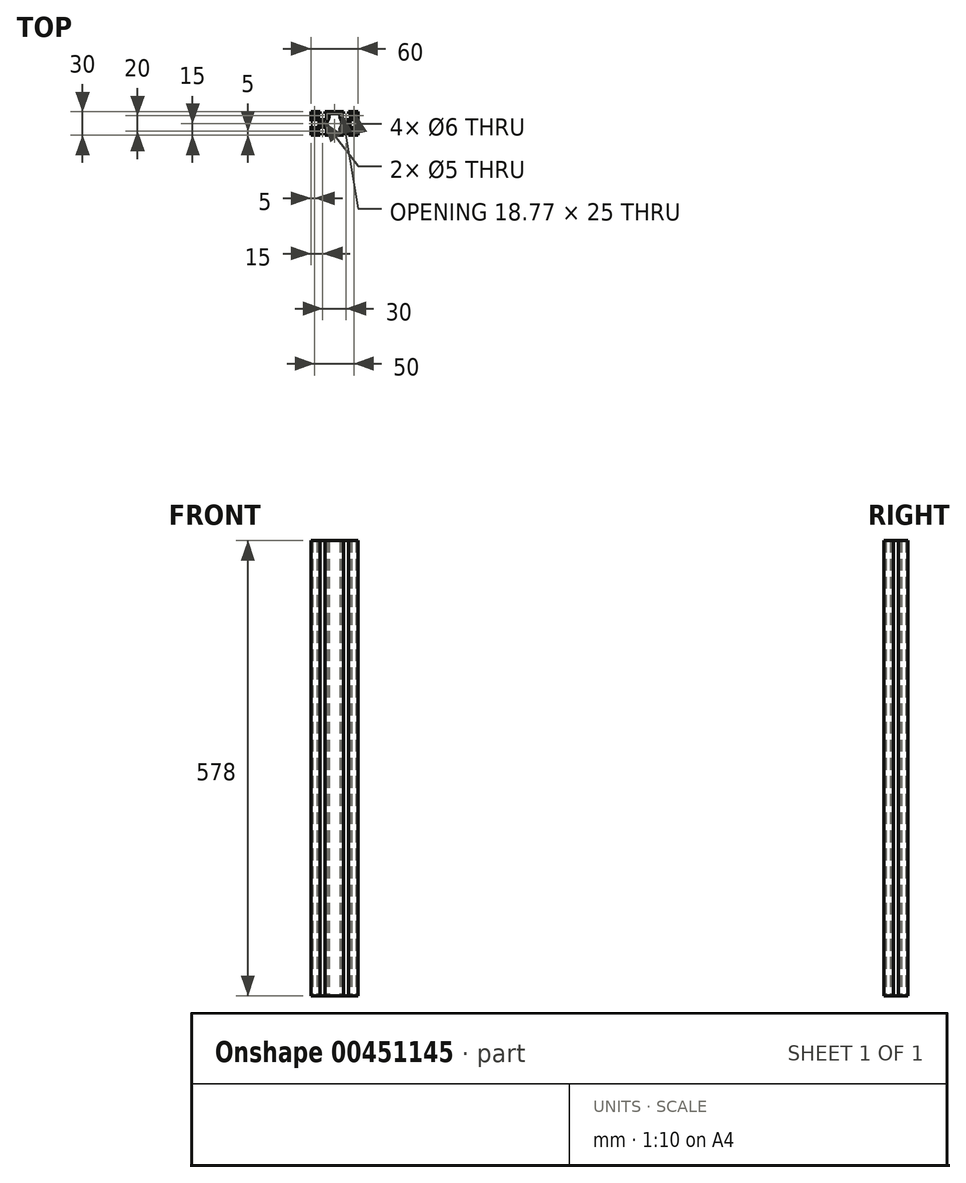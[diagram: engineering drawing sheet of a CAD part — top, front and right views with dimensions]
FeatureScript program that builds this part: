
annotation { "Feature Type Name" : "Feature", "Feature Type Description" : "" }
export const myFeature = defineFeature(function(context is Context, id is Id, definition is map)
    precondition{}
    {
        {
            var Q0;
            Q0=qCreatedBy(makeId("Top.planeOp"),FACE);
            var sketch = newSketch(context, id + "F0", { "sketchPlane" : qUnion([Q0])});
            skLineSegment(sketch, "E0.bottom", {"start": v(30, -15) * mm, "end": v(-30, -15) * mm});
            skLineSegment(sketch, "E0.top", {"start": v(30, 15) * mm, "end": v(-30, 15) * mm});
            skLineSegment(sketch, "E0.left", {"start": v(30, -15) * mm, "end": v(30, 15) * mm});
            skLineSegment(sketch, "E0.right", {"start": v(-30, -15) * mm, "end": v(-30, 15) * mm});
            skPoint(sketch, "E0.middle", {"position": v(0, 0) * mm});
            skLineSegment(sketch, "E1.top", {"start": v(-11.85, 15) * mm, "end": v(-18.15, 15) * mm});
            skLineSegment(sketch, "E1.left", {"start": v(-11.85, 12.5) * mm, "end": v(-11.85, 15) * mm});
            skLineSegment(sketch, "E1.right", {"start": v(-18.15, 12.5) * mm, "end": v(-18.15, 15) * mm});
            skPoint(sketch, "E1.middle", {"position": v(-15, 13.75) * mm});
            skLineSegment(sketch, "E2.bottom", {"start": v(-9.85, 12.5) * mm, "end": v(-11.85, 12.5) * mm});
            skLineSegment(sketch, "E2.left", {"start": v(-9.85, 12.5) * mm, "end": v(-9.85, 6.55) * mm});
            skLineSegment(sketch, "E2.right", {"start": v(-20.15, 12.5) * mm, "end": v(-20.15, 6.55) * mm});
            skPoint(sketch, "E2.middle", {"position": v(-15, 9.52) * mm});
            skArc(sketch, "E3", {"start": v(-20.15, 6.55) * mm, "mid": v(-15, 4.5) * mm, "end": v(-9.85, 6.55) * mm});
            skPoint(sketch, "E4.MirrorP", {"position": v(15, 9.52) * mm});
            skPoint(sketch, "E5.MirrorP", {"position": v(15, 13.75) * mm});
            skLineSegment(sketch, "E6.MirrorCS", {"start": v(11.85, 12.5) * mm, "end": v(11.85, 15) * mm});
            skLineSegment(sketch, "E7.MirrorCS", {"start": v(18.15, 12.5) * mm, "end": v(18.15, 15) * mm});
            skLineSegment(sketch, "E8.MirrorCS", {"start": v(9.85, 12.5) * mm, "end": v(11.85, 12.5) * mm});
            skLineSegment(sketch, "E9.MirrorCS", {"start": v(9.85, 12.5) * mm, "end": v(9.85, 6.55) * mm});
            skArc(sketch, "E10.MirrorCS", {"start": v(20.15, 6.55) * mm, "mid": v(15, 4.5) * mm, "end": v(9.85, 6.55) * mm});
            skLineSegment(sketch, "E11.MirrorCS", {"start": v(20.15, 12.5) * mm, "end": v(20.15, 6.55) * mm});
            skLineSegment(sketch, "E12.MirrorCS", {"start": v(11.85, 15) * mm, "end": v(18.15, 15) * mm});
            skLineSegment(sketch, "E13.trimOffspring", {"start": v(-18.15, 12.5) * mm, "end": v(-20.15, 12.5) * mm});
            skLineSegment(sketch, "E14.trimOffspring", {"start": v(18.15, 12.5) * mm, "end": v(20.15, 12.5) * mm});
            skCircle(sketch, "E15", {"center": v(-15, 0) * mm, "radius": 2.5 * mm});
            skCircle(sketch, "E16", {"center": v(-25, 10) * mm, "radius": 3 * mm});
            skCircle(sketch, "E17.MirrorC", {"center": v(25, 10) * mm, "radius": 3 * mm});
            skCircle(sketch, "E18.MirrorC", {"center": v(25, -10) * mm, "radius": 3 * mm});
            skCircle(sketch, "E19.MirrorC", {"center": v(-25, -10) * mm, "radius": 3 * mm});
            skCircle(sketch, "E20.MirrorC", {"center": v(15, 0) * mm, "radius": 2.5 * mm});
            skLineSegment(sketch, "E21", {"start": v(-7, 12.5) * mm, "end": v(0, 12.5) * mm});
            skLineSegment(sketch, "E22", {"start": v(-7, 12.5) * mm, "end": v(-7, 7) * mm});
            skLineSegment(sketch, "E23", {"start": v(-10, 0) * mm, "end": v(-7, 7) * mm});
            skLineSegment(sketch, "E24.MirrorCS", {"start": v(10, 0) * mm, "end": v(7, 7) * mm});
            skLineSegment(sketch, "E25.MirrorCS", {"start": v(7, 12.5) * mm, "end": v(0, 12.5) * mm});
            skLineSegment(sketch, "E26.MirrorCS", {"start": v(7, 12.5) * mm, "end": v(7, 7) * mm});
            skLineSegment(sketch, "E27.MirrorCS", {"start": v(-18.15, -12.5) * mm, "end": v(-20.15, -12.5) * mm});
            skLineSegment(sketch, "E28.MirrorCS", {"start": v(-9.85, -12.5) * mm, "end": v(-11.85, -12.5) * mm});
            skLineSegment(sketch, "E29.MirrorCS", {"start": v(-9.85, -12.5) * mm, "end": v(-9.85, -6.55) * mm});
            skPoint(sketch, "E30.MirrorP", {"position": v(-15, -13.75) * mm});
            skPoint(sketch, "E31.MirrorP", {"position": v(-15, -9.52) * mm});
            skLineSegment(sketch, "E32.MirrorCS", {"start": v(-18.15, -12.5) * mm, "end": v(-18.15, -15) * mm});
            skLineSegment(sketch, "E33.MirrorCS", {"start": v(-11.85, -15) * mm, "end": v(-18.15, -15) * mm});
            skLineSegment(sketch, "E34.MirrorCS", {"start": v(-20.15, -12.5) * mm, "end": v(-20.15, -6.55) * mm});
            skLineSegment(sketch, "E35.MirrorCS", {"start": v(-11.85, -12.5) * mm, "end": v(-11.85, -15) * mm});
            skArc(sketch, "E36.MirrorCS", {"start": v(-20.15, -6.55) * mm, "mid": v(-15, -4.5) * mm, "end": v(-9.85, -6.55) * mm});
            skLineSegment(sketch, "E37.MirrorCS", {"start": v(18.15, -12.5) * mm, "end": v(20.15, -12.5) * mm});
            skLineSegment(sketch, "E38.MirrorCS", {"start": v(9.85, -12.5) * mm, "end": v(11.85, -12.5) * mm});
            skPoint(sketch, "E39.MirrorP", {"position": v(15, -13.75) * mm});
            skPoint(sketch, "E40.MirrorP", {"position": v(15, -9.52) * mm});
            skLineSegment(sketch, "E41.MirrorCS", {"start": v(18.15, -12.5) * mm, "end": v(18.15, -15) * mm});
            skArc(sketch, "E42.MirrorCS", {"start": v(20.15, -6.55) * mm, "mid": v(15, -4.5) * mm, "end": v(9.85, -6.55) * mm});
            skLineSegment(sketch, "E43.MirrorCS", {"start": v(9.85, -12.5) * mm, "end": v(9.85, -6.55) * mm});
            skLineSegment(sketch, "E44.MirrorCS", {"start": v(11.85, -12.5) * mm, "end": v(11.85, -15) * mm});
            skLineSegment(sketch, "E45.MirrorCS", {"start": v(11.85, -15) * mm, "end": v(18.15, -15) * mm});
            skLineSegment(sketch, "E46.MirrorCS", {"start": v(20.15, -12.5) * mm, "end": v(20.15, -6.55) * mm});
            skLineSegment(sketch, "E47.MirrorCS", {"start": v(10, 0) * mm, "end": v(7, -7) * mm});
            skLineSegment(sketch, "E48.MirrorCS", {"start": v(7, -12.5) * mm, "end": v(7, -7) * mm});
            skLineSegment(sketch, "E49.MirrorCS", {"start": v(7, -12.5) * mm, "end": v(0, -12.5) * mm});
            skLineSegment(sketch, "E50.MirrorCS", {"start": v(-7, -12.5) * mm, "end": v(0, -12.5) * mm});
            skLineSegment(sketch, "E51.MirrorCS", {"start": v(-10, 0) * mm, "end": v(-7, -7) * mm});
            skLineSegment(sketch, "E52.MirrorCS", {"start": v(-7, -12.5) * mm, "end": v(-7, -7) * mm});
            skLineSegment(sketch, "E53.top", {"start": v(-30, 3.15) * mm, "end": v(-30, -3.15) * mm});
            skLineSegment(sketch, "E53.left", {"start": v(-27.5, 3.15) * mm, "end": v(-30, 3.15) * mm});
            skLineSegment(sketch, "E53.right", {"start": v(-27.5, -3.15) * mm, "end": v(-30, -3.15) * mm});
            skLineSegment(sketch, "E54.bottom", {"start": v(-27.5, 5.15) * mm, "end": v(-27.5, 3.15) * mm});
            skLineSegment(sketch, "E54.left", {"start": v(-27.5, 5.15) * mm, "end": v(-21.55, 5.15) * mm});
            skLineSegment(sketch, "E54.right", {"start": v(-27.5, -5.15) * mm, "end": v(-21.55, -5.15) * mm});
            skArc(sketch, "E55", {"start": v(-21.55, -5.15) * mm, "mid": v(-19.5, 0) * mm, "end": v(-21.55, 5.15) * mm});
            skLineSegment(sketch, "E56.trimOffspring", {"start": v(-27.5, -3.15) * mm, "end": v(-27.5, -5.15) * mm});
            skArc(sketch, "E57.MirrorCS", {"start": v(21.55, -5.15) * mm, "mid": v(19.5, 0) * mm, "end": v(21.55, 5.15) * mm});
            skLineSegment(sketch, "E58.MirrorCS", {"start": v(27.5, -5.15) * mm, "end": v(21.55, -5.15) * mm});
            skLineSegment(sketch, "E59.MirrorCS", {"start": v(30, 3.15) * mm, "end": v(30, -3.15) * mm});
            skLineSegment(sketch, "E60.MirrorCS", {"start": v(27.5, -3.15) * mm, "end": v(30, -3.15) * mm});
            skLineSegment(sketch, "E61.MirrorCS", {"start": v(27.5, 5.15) * mm, "end": v(27.5, 3.15) * mm});
            skLineSegment(sketch, "E62.MirrorCS", {"start": v(27.5, 3.15) * mm, "end": v(30, 3.15) * mm});
            skLineSegment(sketch, "E63.MirrorCS", {"start": v(27.5, 5.15) * mm, "end": v(21.55, 5.15) * mm});
            skLineSegment(sketch, "E64.MirrorCS", {"start": v(27.5, -3.15) * mm, "end": v(27.5, -5.15) * mm});
            skSolve(sketch);
        }
        {
            var Q0;
            {var subQ30=sQuery(id+"F0.wireOp",EDGE,"E1.left");Q0=makeQuery(id+"F0.imprint","IMPRINT",FACE,{"disambiguationData":[TD([[makeQuery(id+"F0.imprint","IMPRINT",EDGE,{"derivedFrom":subQ30}),-1.0]])]});}
            extrude(context, id + "F1", {"entities" : qUnion([Q0]), "offsetDistance" : 25 * mm, "depth" : 578 * mm});
        }
        {
            var Q0;
            Q0=makeQuery(id+"F1.opExtrude","SWEPT_EDGE",EDGE,{"disambiguationData":[OSD([sQuery(id+"F0.wireOp",EDGE,"E21"),sQuery(id+"F0.wireOp",EDGE,"E22")])]});
            var Q1;
            Q1=makeQuery(id+"F1.opExtrude","SWEPT_EDGE",EDGE,{"disambiguationData":[OSD([sQuery(id+"F0.wireOp",EDGE,"E25.MirrorCS"),sQuery(id+"F0.wireOp",EDGE,"E26.MirrorCS")])]});
            var Q2;
            Q2=makeQuery(id+"F1.opExtrude","SWEPT_EDGE",EDGE,{"disambiguationData":[OSD([sQuery(id+"F0.wireOp",EDGE,"840db5bc-c403-45cd-90c7-254e62d9e8c5.3.2"),sQuery(id+"F0.wireOp",EDGE,"840db5bc-c403-45cd-90c7-254e62d9e8c5.3.3")])]});
            var Q3;
            Q3=makeQuery(id+"F1.opExtrude","SWEPT_EDGE",EDGE,{"disambiguationData":[OSD([sQuery(id+"F0.wireOp",EDGE,"840db5bc-c403-45cd-90c7-254e62d9e8c5.3.4"),sQuery(id+"F0.wireOp",EDGE,"840db5bc-c403-45cd-90c7-254e62d9e8c5.3.5")])]});
            var Q4;
            Q4=makeQuery(id+"F1.opExtrude","SWEPT_EDGE",EDGE,{"disambiguationData":[OSD([sQuery(id+"F0.wireOp",EDGE,"840db5bc-c403-45cd-90c7-254e62d9e8c5.1.4"),sQuery(id+"F0.wireOp",EDGE,"840db5bc-c403-45cd-90c7-254e62d9e8c5.1.5")])]});
            var Q5;
            Q5=makeQuery(id+"F1.opExtrude","SWEPT_EDGE",EDGE,{"disambiguationData":[OSD([sQuery(id+"F0.wireOp",EDGE,"840db5bc-c403-45cd-90c7-254e62d9e8c5.1.2"),sQuery(id+"F0.wireOp",EDGE,"840db5bc-c403-45cd-90c7-254e62d9e8c5.1.3")])]});
            var Q6;
            Q6=makeQuery(id+"F1.opExtrude","SWEPT_EDGE",EDGE,{"disambiguationData":[OSD([sQuery(id+"F0.wireOp",EDGE,"840db5bc-c403-45cd-90c7-254e62d9e8c5.2.2"),sQuery(id+"F0.wireOp",EDGE,"840db5bc-c403-45cd-90c7-254e62d9e8c5.2.3")])]});
            var Q7;
            Q7=makeQuery(id+"F1.opExtrude","SWEPT_EDGE",EDGE,{"disambiguationData":[OSD([sQuery(id+"F0.wireOp",EDGE,"840db5bc-c403-45cd-90c7-254e62d9e8c5.2.4"),sQuery(id+"F0.wireOp",EDGE,"840db5bc-c403-45cd-90c7-254e62d9e8c5.2.5")])]});
            fillet(context, id + "F2", {"entities" : qUnion([Q0, Q1, Q2, Q3, Q4, Q5, Q6, Q7]), "radius" : 2 * mm, "tangentPropagation" : true, "allowEdgeOverflow" : false});
        }
        {
            var Q0;
            Q0=makeQuery(id+"F1.opExtrude","SWEPT_EDGE",EDGE,{"disambiguationData":[OSD([sQuery(id+"F0.wireOp",EDGE,"DFmKlNwq-wdCH-8nxe-YtyU-4GV9lN6q6mBF"),sQuery(id+"F0.wireOp",EDGE,"E23")])]});
            var Q1;
            Q1=makeQuery(id+"F1.opExtrude","SWEPT_EDGE",EDGE,{"disambiguationData":[OSD([sQuery(id+"F0.wireOp",EDGE,"666cdc41-9f22-4022-b962-67eb0134baf70.MirrorCS"),sQuery(id+"F0.wireOp",EDGE,"E24.MirrorCS")])]});
            var Q2;
            Q2=makeQuery(id+"F1.opExtrude","SWEPT_EDGE",EDGE,{"disambiguationData":[OSD([sQuery(id+"F0.wireOp",EDGE,"840db5bc-c403-45cd-90c7-254e62d9e8c5.3.0"),sQuery(id+"F0.wireOp",EDGE,"840db5bc-c403-45cd-90c7-254e62d9e8c5.3.1")])]});
            var Q3;
            Q3=makeQuery(id+"F1.opExtrude","SWEPT_EDGE",EDGE,{"disambiguationData":[OSD([sQuery(id+"F0.wireOp",EDGE,"840db5bc-c403-45cd-90c7-254e62d9e8c5.1.6"),sQuery(id+"F0.wireOp",EDGE,"840db5bc-c403-45cd-90c7-254e62d9e8c5.1.7")])]});
            var Q4;
            Q4=makeQuery(id+"F1.opExtrude","SWEPT_EDGE",EDGE,{"disambiguationData":[OSD([sQuery(id+"F0.wireOp",EDGE,"840db5bc-c403-45cd-90c7-254e62d9e8c5.1.0"),sQuery(id+"F0.wireOp",EDGE,"840db5bc-c403-45cd-90c7-254e62d9e8c5.1.1")])]});
            var Q5;
            Q5=makeQuery(id+"F1.opExtrude","SWEPT_EDGE",EDGE,{"disambiguationData":[OSD([sQuery(id+"F0.wireOp",EDGE,"840db5bc-c403-45cd-90c7-254e62d9e8c5.3.6"),sQuery(id+"F0.wireOp",EDGE,"840db5bc-c403-45cd-90c7-254e62d9e8c5.3.7")])]});
            var Q6;
            Q6=makeQuery(id+"F1.opExtrude","SWEPT_EDGE",EDGE,{"disambiguationData":[OSD([sQuery(id+"F0.wireOp",EDGE,"840db5bc-c403-45cd-90c7-254e62d9e8c5.2.0"),sQuery(id+"F0.wireOp",EDGE,"840db5bc-c403-45cd-90c7-254e62d9e8c5.2.1")])]});
            var Q7;
            Q7=makeQuery(id+"F1.opExtrude","SWEPT_EDGE",EDGE,{"disambiguationData":[OSD([sQuery(id+"F0.wireOp",EDGE,"840db5bc-c403-45cd-90c7-254e62d9e8c5.2.6"),sQuery(id+"F0.wireOp",EDGE,"840db5bc-c403-45cd-90c7-254e62d9e8c5.2.7")])]});
            fillet(context, id + "F3", {"entities" : qUnion([Q0, Q1, Q2, Q3, Q4, Q5, Q6, Q7]), "radius" : 7 * mm, "tangentPropagation" : true, "allowEdgeOverflow" : false});
        }
    });
